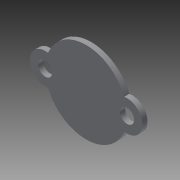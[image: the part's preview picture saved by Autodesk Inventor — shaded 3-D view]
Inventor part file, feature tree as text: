
AUTODESK INVENTOR PART (.ipt)
format: ipt  version: 2014 (Build 180170000, 170)  size: 107,520 bytes
history: native  units: mm
features: extrude x3, sketch x3
ambient origin geometry x8: Origin, YZ Plane, XZ Plane, XY Plane, X Axis, Y Axis, Z Axis, Center Point
bodies: Volumenkörper1 (feature_tree)
feature tree (6):
  extrude  "Extrusion1"  Depth=6.0mm
  extrude  "Extrusion2"  Depth=1.0mm TaperAngle=0.0deg
  extrude  "Extrusion3"  Depth=0.5mm
  sketch  "Skizze1"  dims[d0=16.0mm d1=6.0mm]
  sketch  "Skizze2"  dims[d2=6.0mm d3=1.0mm d4=0.0mm]
  sketch  "Skizze3"  dims[d5=11.75mm d6=9.0mm d7=0.5mm d8=0.0mm d9=2.75mm d10=2.75mm d11=0.5mm d12=0.0mm]
